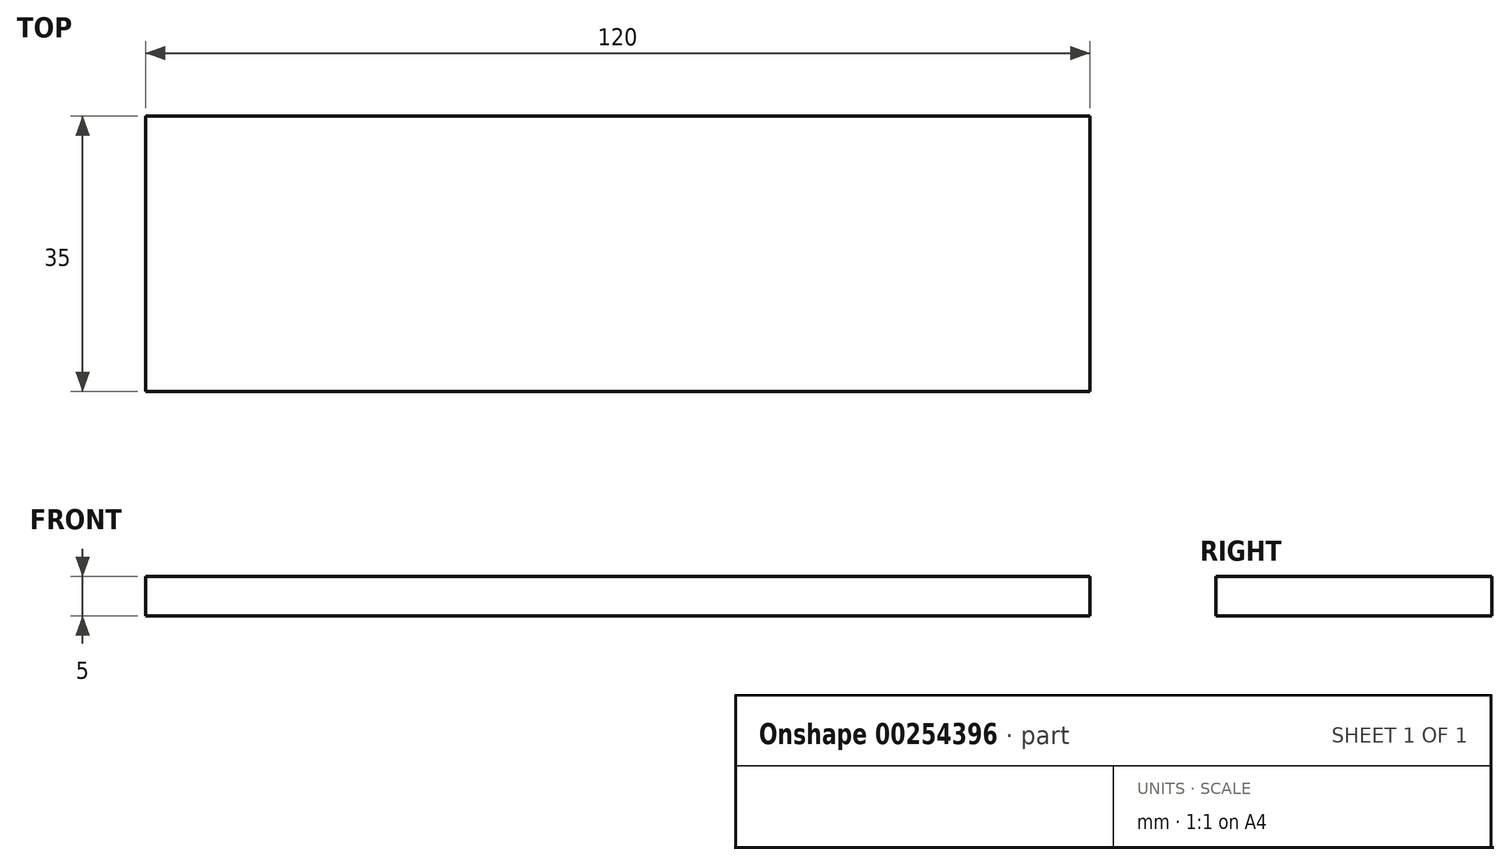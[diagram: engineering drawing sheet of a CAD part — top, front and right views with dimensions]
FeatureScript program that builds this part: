
annotation { "Feature Type Name" : "Feature", "Feature Type Description" : "" }
export const myFeature = defineFeature(function(context is Context, id is Id, definition is map)
    precondition{}
    {
        {
            var Q0;
            Q0=qCreatedBy(makeId("Top.planeOp"),FACE);
            var sketch = newSketch(context, id + "F0", { "sketchPlane" : qUnion([Q0])});
            skLineSegment(sketch, "E0.bottom", {"start": v(60, 17.5) * mm, "end": v(-60, 17.5) * mm});
            skLineSegment(sketch, "E0.top", {"start": v(60, -17.5) * mm, "end": v(-60, -17.5) * mm});
            skLineSegment(sketch, "E0.left", {"start": v(60, 17.5) * mm, "end": v(60, -17.5) * mm});
            skLineSegment(sketch, "E0.right", {"start": v(-60, 17.5) * mm, "end": v(-60, -17.5) * mm});
            skPoint(sketch, "E0.middle", {"position": v(0, 0) * mm});
            skSolve(sketch);
        }
        {
            var Q0;
            Q0=makeQuery(id+"F0.imprint","IMPRINT",FACE,{"disambiguationData":[TD([[makeQuery(id+"F0.imprint","IMPRINT",EDGE,{"derivedFrom":sQuery(id+"F0.wireOp",EDGE,"E0.bottom")}),1.0]])]});
            extrude(context, id + "F1", {"entities" : qUnion([Q0]), "depth" : 5 * mm});
        }
    });
